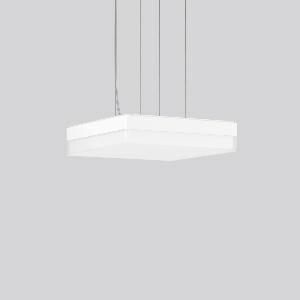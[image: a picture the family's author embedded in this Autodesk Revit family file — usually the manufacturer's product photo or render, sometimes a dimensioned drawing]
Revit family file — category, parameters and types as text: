
# Revit family: flat_slim_square_312541_002_76_8cef
name_source: partatom
category: Lighting Fixtures
units: mm (PartAtom-declared; Revit-internal decimal feet)

## family parameters
Cut with Voids When Loaded = No
Host = Face
Light Source = No
Part Type = Normal
Room Calculation Point = No
Round Connector Dimension = Use Diameter
Shared = No

## types (1)
- MultiLumen 2 840 (1 x LED Modul 840, 2400 lm, 4000)
    Apparent Load = 21 VA
    CIE Flux Codes = 43 74 93 92 100
    Color Rendering = 80
    Color Temperature = 4000
    Default Elevation = 1800 mm
    Height = 70 mm
    Lamp = 1 x LED Modul 840
    Lamp Light Flux = 2400 lm
    Lamp count = 1
    Length = 300 mm
    Lifetime = 50000 h
    Luminous efficacy = 114 lm/W
    Manufacturer = RZB
    ModVariant = No
    Model = 312541.002.76
    Mounting Place = Ceiling
    Mounting Type = Pendant
    Number of Poles = 1
    OnlyDefault = Yes
    Power Factor = 1
    Product Name = FLAT SLIM square
    Product group = Pendant luminaires
    ProductGroupID = 902
    Protection Class = Protection class I
    Protection Degree = IP 40
    RLX_Detail_Level = 1
    RLX_Emergency_Light_Flux = 0 lm
    RLX_Emergency_Type = 0
    RLX_Emergency_Type_DB = No
    RlxData = <blob elided: 14253 chars, md5=c11ee7c5>
    Socket = socket
    Standby Power = 0 W
    System Light Flux = 2400 lm
    System Power = 21 W
    Type Comments = MultiLumen 2 840
    Type Image = 312541.002.jpg
    URL = http://relux.com
    VarID = multilumen_2_840
    Voltage = 230 V
    Voltage Range = 220-240 V
    Weight = 0.00 kg
    Width = 300 mm

## geometry (parser evidence)
native form markers: Sweep x11
no freeform markers — native parametric forms only
